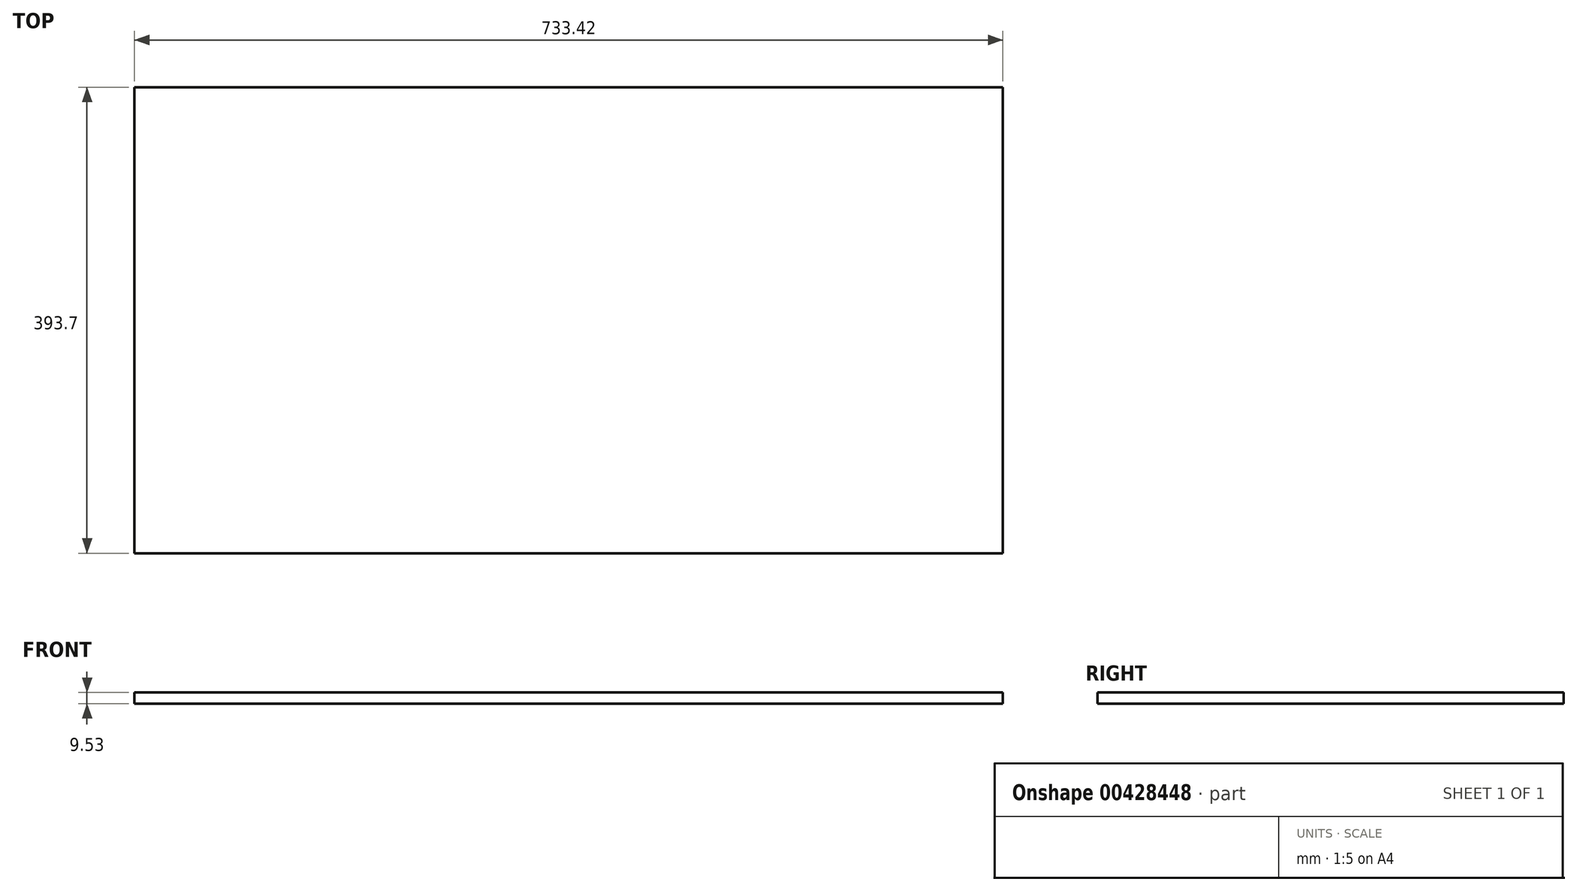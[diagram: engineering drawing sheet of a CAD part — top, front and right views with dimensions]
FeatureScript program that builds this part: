
annotation { "Feature Type Name" : "Feature", "Feature Type Description" : "" }
export const myFeature = defineFeature(function(context is Context, id is Id, definition is map)
    precondition{}
    {
        {
            var Q0;
            Q0=qCreatedBy(makeId("Top.planeOp"),FACE);
            var sketch = newSketch(context, id + "F0", { "sketchPlane" : qUnion([Q0])});
            skLineSegment(sketch, "E0.bottom", {"start": v(366.71, -196.85) * mm, "end": v(-366.71, -196.85) * mm});
            skLineSegment(sketch, "E0.top", {"start": v(366.71, 196.85) * mm, "end": v(-366.71, 196.85) * mm});
            skLineSegment(sketch, "E0.left", {"start": v(366.71, -196.85) * mm, "end": v(366.71, 196.85) * mm});
            skLineSegment(sketch, "E0.right", {"start": v(-366.71, -196.85) * mm, "end": v(-366.71, 196.85) * mm});
            skPoint(sketch, "E0.middle", {"position": v(0, 0) * mm});
            skSolve(sketch);
        }
        {
            var Q0;
            Q0=makeQuery(id+"F0.imprint","IMPRINT",FACE,{"disambiguationData":[TD([[makeQuery(id+"F0.imprint","IMPRINT",EDGE,{"derivedFrom":sQuery(id+"F0.wireOp",EDGE,"E0.bottom")}),-1.0]])]});
            extrude(context, id + "F1", {"entities" : qUnion([Q0]), "depth" : 9.52 * mm});
        }
    });
